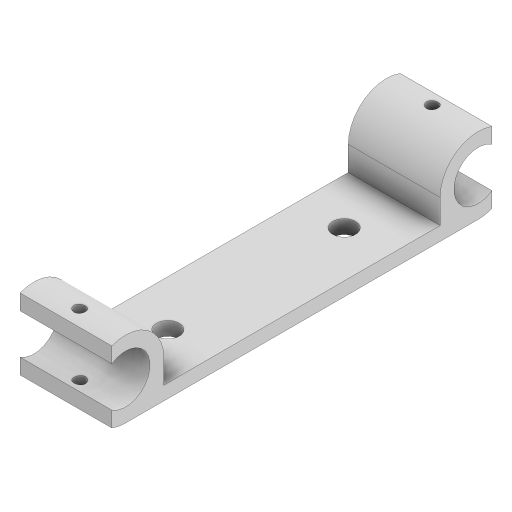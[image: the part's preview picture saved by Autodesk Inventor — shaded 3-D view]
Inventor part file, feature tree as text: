
AUTODESK INVENTOR PART (.ipt)
format: ipt  version: 2023 (Build 270158000, 158)  size: 180,736 bytes
history: native  units: mm
features: extrude x3, projected_geometry x3, other x2, sketch x2
ambient origin geometry x8: Origin, YZ Plane, XZ Plane, XY Plane, X Axis, Y Axis, Z Axis, Center Point
bodies: Body1 (feature_tree)
feature tree (10):
  other  "솔리드1"
  extrude  "돌출1"  Depth=10.6mm
  other  "작업 평면1"
  sketch  "스케치3"
  extrude  "돌출3"  Depth=3.0mm
  extrude  "돌출4"  Depth=10.0mm
  sketch  "스케치1"
  projected_geometry  "투영된 루프2"
  projected_geometry  "투영된 루프3"
  projected_geometry  "투영된 루프4"
